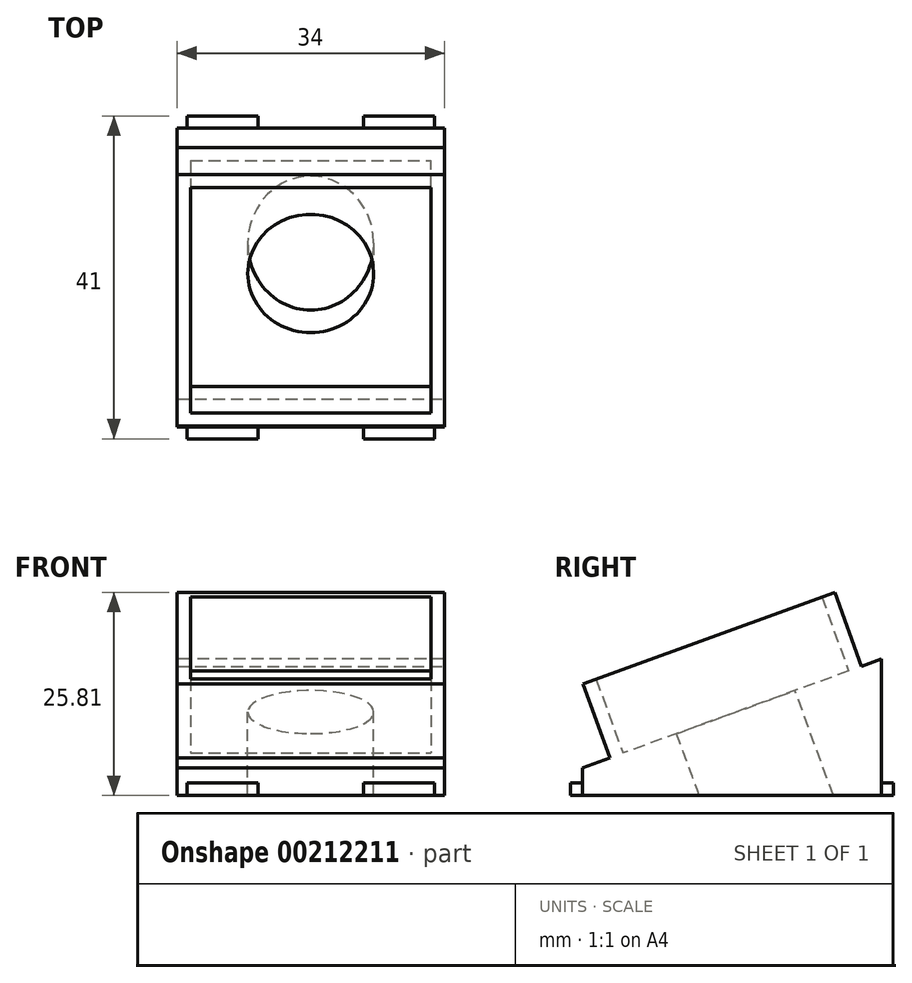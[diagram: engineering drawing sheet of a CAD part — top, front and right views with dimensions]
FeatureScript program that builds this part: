
annotation { "Feature Type Name" : "Feature", "Feature Type Description" : "" }
export const myFeature = defineFeature(function(context is Context, id is Id, definition is map)
    precondition{}
    {
        {
            var Q0;
            Q0=qCreatedBy(makeId("Top.planeOp"),FACE);
            var sketch = newSketch(context, id + "F0", { "sketchPlane" : qUnion([Q0])});
            skLineSegment(sketch, "E0.bottom", {"start": v(-17, 19) * mm, "end": v(-15.7, 19) * mm});
            skLineSegment(sketch, "E0.top", {"start": v(-17, -19) * mm, "end": v(-15.7, -19) * mm});
            skLineSegment(sketch, "E0.left", {"start": v(-17, 19) * mm, "end": v(-17, -19) * mm});
            skLineSegment(sketch, "E0.right", {"start": v(17, 19) * mm, "end": v(17, -19) * mm});
            skLineSegment(sketch, "E1", {"start": v(-15.7, 19) * mm, "end": v(-15.7, 20.5) * mm});
            skLineSegment(sketch, "E2", {"start": v(-15.7, 20.5) * mm, "end": v(-6.7, 20.5) * mm});
            skLineSegment(sketch, "E3", {"start": v(-6.7, 20.5) * mm, "end": v(-6.7, 19) * mm});
            skLineSegment(sketch, "E4.trimOffspring", {"start": v(-6.7, 19) * mm, "end": v(6.7, 19) * mm});
            skLineSegment(sketch, "E5.MirrorCS", {"start": v(6.7, 20.5) * mm, "end": v(6.7, 19) * mm});
            skLineSegment(sketch, "E6.MirrorCS", {"start": v(15.7, 20.5) * mm, "end": v(6.7, 20.5) * mm});
            skLineSegment(sketch, "E7.MirrorCS", {"start": v(17, 19) * mm, "end": v(15.7, 19) * mm});
            skLineSegment(sketch, "E8.MirrorCS", {"start": v(15.7, 19) * mm, "end": v(15.7, 20.5) * mm});
            skLineSegment(sketch, "E9.MirrorCS", {"start": v(15.7, -19) * mm, "end": v(15.7, -20.5) * mm});
            skLineSegment(sketch, "E10.MirrorCS", {"start": v(15.7, -20.5) * mm, "end": v(6.7, -20.5) * mm});
            skLineSegment(sketch, "E11.MirrorCS", {"start": v(6.7, -20.5) * mm, "end": v(6.7, -19) * mm});
            skLineSegment(sketch, "E12.MirrorCS", {"start": v(-6.7, -20.5) * mm, "end": v(-6.7, -19) * mm});
            skLineSegment(sketch, "E13.MirrorCS", {"start": v(-15.7, -20.5) * mm, "end": v(-6.7, -20.5) * mm});
            skLineSegment(sketch, "E14.MirrorCS", {"start": v(-15.7, -19) * mm, "end": v(-15.7, -20.5) * mm});
            skLineSegment(sketch, "E15.trimOffspring", {"start": v(-6.7, -19) * mm, "end": v(6.7, -19) * mm});
            skLineSegment(sketch, "E16.trimOffspring", {"start": v(15.7, -19) * mm, "end": v(17, -19) * mm});
            skSolve(sketch);
        }
        {
            var Q0;
            Q0=makeQuery(id+"F0.imprint","IMPRINT",FACE,{"disambiguationData":[TD([[makeQuery(id+"F0.imprint","IMPRINT",EDGE,{"derivedFrom":sQuery(id+"F0.wireOp",EDGE,"U1Lrzj9K-po7K-0BUD-hQei-LFnklX6tutFy")}),-1.0]])]});
            var Q1;
            Q1=makeQuery(id+"F0.imprint","IMPRINT",FACE,{"disambiguationData":[TD([[makeQuery(id+"F0.imprint","IMPRINT",EDGE,{"derivedFrom":sQuery(id+"F0.wireOp",EDGE,"E0.bottom")}),-1.0]])]});
            extrude(context, id + "F1", {"entities" : qUnion([Q0, Q1]), "depth" : 1.6 * mm});
        }
        {
            var Q0;
            Q0=makeQuery(id+"F1.opExtrude","CAP_FACE",FACE,{"disambiguationData":[OSD([sQuery(id+"F0.wireOp",EDGE,"E0.bottom"),sQuery(id+"F0.wireOp",EDGE,"E0.left"),sQuery(id+"F0.wireOp",EDGE,"E0.right"),sQuery(id+"F0.wireOp",EDGE,"E1"),sQuery(id+"F0.wireOp",EDGE,"E2"),sQuery(id+"F0.wireOp",EDGE,"E3"),sQuery(id+"F0.wireOp",EDGE,"E4.trimOffspring"),sQuery(id+"F0.wireOp",EDGE,"E5.MirrorCS"),sQuery(id+"F0.wireOp",EDGE,"E6.MirrorCS"),sQuery(id+"F0.wireOp",EDGE,"E7.MirrorCS"),sQuery(id+"F0.wireOp",EDGE,"E8.MirrorCS"),sQuery(id+"F0.wireOp",EDGE,"E9.MirrorCS"),sQuery(id+"F0.wireOp",EDGE,"E10.MirrorCS"),sQuery(id+"F0.wireOp",EDGE,"E11.MirrorCS"),sQuery(id+"F0.wireOp",EDGE,"E12.MirrorCS"),sQuery(id+"F0.wireOp",EDGE,"E13.MirrorCS"),sQuery(id+"F0.wireOp",EDGE,"E0.top"),sQuery(id+"F0.wireOp",EDGE,"E14.MirrorCS"),sQuery(id+"F0.wireOp",EDGE,"E15.trimOffspring"),sQuery(id+"F0.wireOp",EDGE,"E16.trimOffspring")])],"isStart":false});
            var sketch = newSketch(context, id + "F2", { "sketchPlane" : qUnion([Q0])});
            skLineSegment(sketch, "E17.bottom", {"start": v(-17, 19) * mm, "end": v(17, 19) * mm});
            skLineSegment(sketch, "E17.top", {"start": v(-17, -19) * mm, "end": v(17, -19) * mm});
            skLineSegment(sketch, "E17.left", {"start": v(-17, 19) * mm, "end": v(-17, -19) * mm});
            skLineSegment(sketch, "E17.right", {"start": v(17, 19) * mm, "end": v(17, -19) * mm});
            skSolve(sketch);
        }
        {
            var Q0;
            {var subQ6=sQuery(id+"F2.wireOp",EDGE,"E17.left");Q0=makeQuery(id+"F2.imprint","IMPRINT",FACE,{"disambiguationData":[TD([[makeQuery(id+"F2.imprint","IMPRINT",EDGE,{"derivedFrom":subQ6}),1.0]])]});}
            extrude(context, id + "F3", {"entities" : qUnion([Q0]), "operationType" : NewBodyOperationType.ADD, "depth" : 20 * mm});
        }
        {
            var Q0;
            Q0=makeQuery(id+"F3.boolean.opBoolean","MERGE",FACE,{"derivedFrom":[makeQuery(id+"F1.opExtrude","SWEPT_FACE",FACE,{"disambiguationData":[OSD([sQuery(id+"F0.wireOp",EDGE,"E0.left")])]}),makeQuery(id+"F3.opExtrude","SWEPT_FACE",FACE,{"disambiguationData":[OSD([sQuery(id+"F2.wireOp",EDGE,"E17.left")])]})]});
            var sketch = newSketch(context, id + "F4", { "sketchPlane" : qUnion([Q0])});
            skLineSegment(sketch, "E18", {"start": v(19, 3.5) * mm, "end": v(-19, 17.33) * mm});
            skLineSegment(sketch, "E19", {"start": v(19, 3.5) * mm, "end": v(-19, 3.5) * mm, "construction": true});
            skLineSegment(sketch, "E20", {"start": v(-19, 17.33) * mm, "end": v(-19, 21.6) * mm});
            skLineSegment(sketch, "E21", {"start": v(-19, 21.6) * mm, "end": v(19, 21.6) * mm});
            skLineSegment(sketch, "E22", {"start": v(19, 21.6) * mm, "end": v(19, 3.5) * mm});
            skSolve(sketch);
        }
        {
            var Q0;
            Q0=makeQuery(id+"F4.imprint","IMPRINT",FACE,{"disambiguationData":[TD([[makeQuery(id+"F4.imprint","IMPRINT",EDGE,{"derivedFrom":sQuery(id+"F4.wireOp",EDGE,"E18")}),-1.0]])]});
            extrude(context, id + "F5", {"entities" : qUnion([Q0]), "operationType" : NewBodyOperationType.REMOVE, "endBound" : BoundingType.THROUGH_ALL, "oppositeDirection" : true, "depth" : 25 * mm});
        }
        {
            var Q0;
            Q0=makeQuery(id+"F5.boolean.opBoolean","COPY",FACE,{"derivedFrom":makeQuery(id+"F5.opExtrude","SWEPT_FACE",FACE,{"disambiguationData":[OSD([sQuery(id+"F4.wireOp",EDGE,"E18")])]})});
            var sketch = newSketch(context, id + "F6", { "sketchPlane" : qUnion([Q0])});
            skLineSegment(sketch, "E23.bottom", {"start": v(-15.25, 19.34) * mm, "end": v(15.25, 19.34) * mm});
            skLineSegment(sketch, "E23.top", {"start": v(-15.25, -11.16) * mm, "end": v(15.25, -11.16) * mm});
            skLineSegment(sketch, "E23.left", {"start": v(-15.25, 19.34) * mm, "end": v(-15.25, -11.16) * mm});
            skLineSegment(sketch, "E23.right", {"start": v(15.25, 19.34) * mm, "end": v(15.25, -11.16) * mm});
            skLineSegment(sketch, "E24.bottom", {"start": v(-17, 21.1) * mm, "end": v(17, 21.1) * mm});
            skLineSegment(sketch, "E24.top", {"start": v(-17, -12.9) * mm, "end": v(17, -12.9) * mm});
            skLineSegment(sketch, "E24.left", {"start": v(-17, 21.1) * mm, "end": v(-17, -12.9) * mm});
            skLineSegment(sketch, "E24.right", {"start": v(17, 21.1) * mm, "end": v(17, -12.9) * mm});
            skCircle(sketch, "E25", {"center": v(0, 4.1) * mm, "radius": 8 * mm});
            skSolve(sketch);
        }
        {
            var Q0;
            Q0=makeQuery(id+"F6.imprint","IMPRINT",FACE,{"disambiguationData":[TD([[makeQuery(id+"F6.imprint","IMPRINT",EDGE,{"derivedFrom":sQuery(id+"F6.wireOp",EDGE,"E23.bottom")}),1.0]])]});
            extrude(context, id + "F7", {"entities" : qUnion([Q0]), "operationType" : NewBodyOperationType.ADD, "depth" : 10 * mm});
        }
        {
            var Q0;
            Q0=makeQuery(id+"F6.imprint","IMPRINT",FACE,{"disambiguationData":[TD([[makeQuery(id+"F6.imprint","IMPRINT",EDGE,{"derivedFrom":sQuery(id+"F6.wireOp",EDGE,"E25")}),1.0]])]});
            extrude(context, id + "F8", {"entities" : qUnion([Q0]), "operationType" : NewBodyOperationType.REMOVE, "endBound" : BoundingType.THROUGH_ALL, "oppositeDirection" : true, "depth" : 25 * mm});
        }
    });
